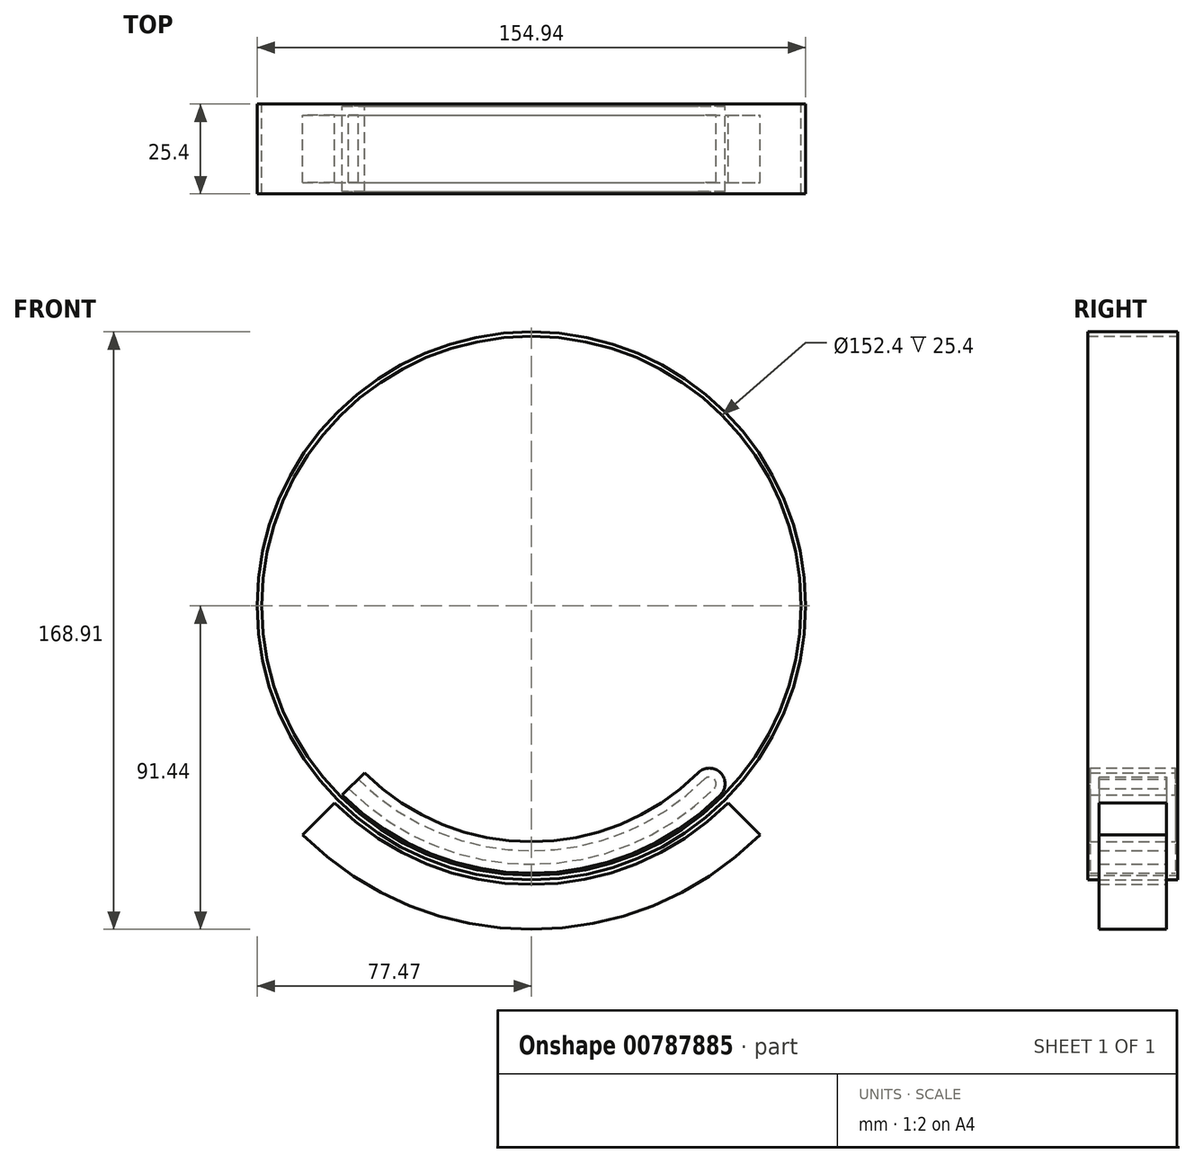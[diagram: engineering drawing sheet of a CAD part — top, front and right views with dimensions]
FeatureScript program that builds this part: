
annotation { "Feature Type Name" : "Feature", "Feature Type Description" : "" }
export const myFeature = defineFeature(function(context is Context, id is Id, definition is map)
    precondition{}
    {
        {
            var Q0;
            Q0=qCreatedBy(makeId("Front.planeOp"),FACE);
            var sketch = newSketch(context, id + "F0", { "sketchPlane" : qUnion([Q0])});
            skCircle(sketch, "E0", {"center": v(0, 0) * mm, "radius": 76.2 * mm});
            skCircle(sketch, "E1", {"center": v(0, 0) * mm, "radius": 77.47 * mm});
            skSolve(sketch);
        }
        {
            var Q0;
            Q0 = qSketchRegion(id + "F0", true);
            extrude(context, id + "F1", {"entities" : qUnion([Q0]), "depth" : 25.4 * mm, "offsetDistance" : 25.4 * mm, "symmetric" : true});
        }
        {
            var Q0;
            Q0=qCreatedBy(makeId("Front.planeOp"),FACE);
            var sketch = newSketch(context, id + "F2", { "sketchPlane" : qUnion([Q0])});
            skLineSegment(sketch, "E2", {"start": v(-48.94, -48.94) * mm, "end": v(-51.64, -51.64) * mm});
            skLineSegment(sketch, "E3", {"start": v(48.94, -48.94) * mm, "end": v(48.94, -48.94) * mm});
            skArc(sketch, "E4", {"start": v(-51.64, -51.64) * mm, "mid": v(0, -73.02) * mm, "end": v(51.64, -51.64) * mm});
            skArc(sketch, "E5", {"start": v(-48.94, -48.94) * mm, "mid": v(0, -69.22) * mm, "end": v(48.94, -48.94) * mm});
            skArc(sketch, "E6", {"start": v(-55.68, -55.68) * mm, "mid": v(0, -78.74) * mm, "end": v(55.68, -55.68) * mm});
            skArc(sketch, "E7", {"start": v(-64.66, -64.66) * mm, "mid": v(0, -91.44) * mm, "end": v(64.66, -64.66) * mm});
            skLineSegment(sketch, "E8.trimOffspring", {"start": v(-55.68, -55.68) * mm, "end": v(-64.66, -64.66) * mm});
            skLineSegment(sketch, "E9.trimOffspring", {"start": v(55.68, -55.68) * mm, "end": v(64.66, -64.66) * mm});
            skArc(sketch, "E10", {"start": v(51.64, -51.64) * mm, "mid": v(51.64, -48.94) * mm, "end": v(48.94, -48.94) * mm});
            skLineSegment(sketch, "E11.trimOffspring", {"start": v(51.64, -51.64) * mm, "end": v(51.64, -51.64) * mm});
            skSolve(sketch);
        }
        {
            var Q0;
            Q0 = qSketchRegion(id + "F2", true);
            extrude(context, id + "F3", {"entities" : qUnion([Q0]), "depth" : 19.05 * mm, "offsetDistance" : 25.4 * mm, "symmetric" : true});
        }
        {
            var Q0;
            Q0=makeQuery(id+"F3.opExtrude","SWEPT_FACE",FACE,{"disambiguationData":[OSD([sQuery(id+"F2.wireOp",EDGE,"E2")])]});
            shell(context, id + "F4", {"entities" : qUnion([Q0]), "thickness" : 2.54 * mm, "oppositeDirection" : true});
        }
    });
